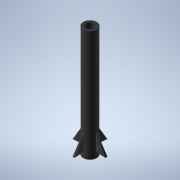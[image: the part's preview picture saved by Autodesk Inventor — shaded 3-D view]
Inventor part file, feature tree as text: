
AUTODESK INVENTOR PART (.ipt)
format: ipt  version: 2022 (Build 260153000, 153)  size: 240,128 bytes
history: native  units: in
note: dims shown in document units (in); Inventor stores cm internally (conversion verified against a paired STEP export)
features: revolve x2, fillet x2, sketch x2, pattern_circular x1
ambient origin geometry x8: Origin, YZ Plane, XZ Plane, XY Plane, X Axis, Y Axis, Z Axis, Center Point
bodies: Solid1 (feature_tree)
feature tree (7):
  revolve  "Revolution1"  [1 undecoded]
  revolve  "Revolution3"  [1 undecoded]
  pattern_circular  "Circular Pattern1"  Angle=90.0deg  [1 undecoded]
  fillet  "Fillet1"  Radius=0.5906in
  fillet  "Fillet2"  [1 undecoded]
  sketch  "Sketch2"  dims[d0=3.937in d1=0.315in]
  sketch  "Sketch4"  dims[d2=3.937in d3=0.4724in d4=90.0deg d10=0.5906in d11=30.0deg d12=0.0687in d13=1.5748in d14=360.0deg d16=0.0197in d17=0.0197in]
note: 4 required parameter values undecoded (feature->parameter linkage not recoverable at this tier; creation-order binding heuristic only, values carry confidence <= 0.55)